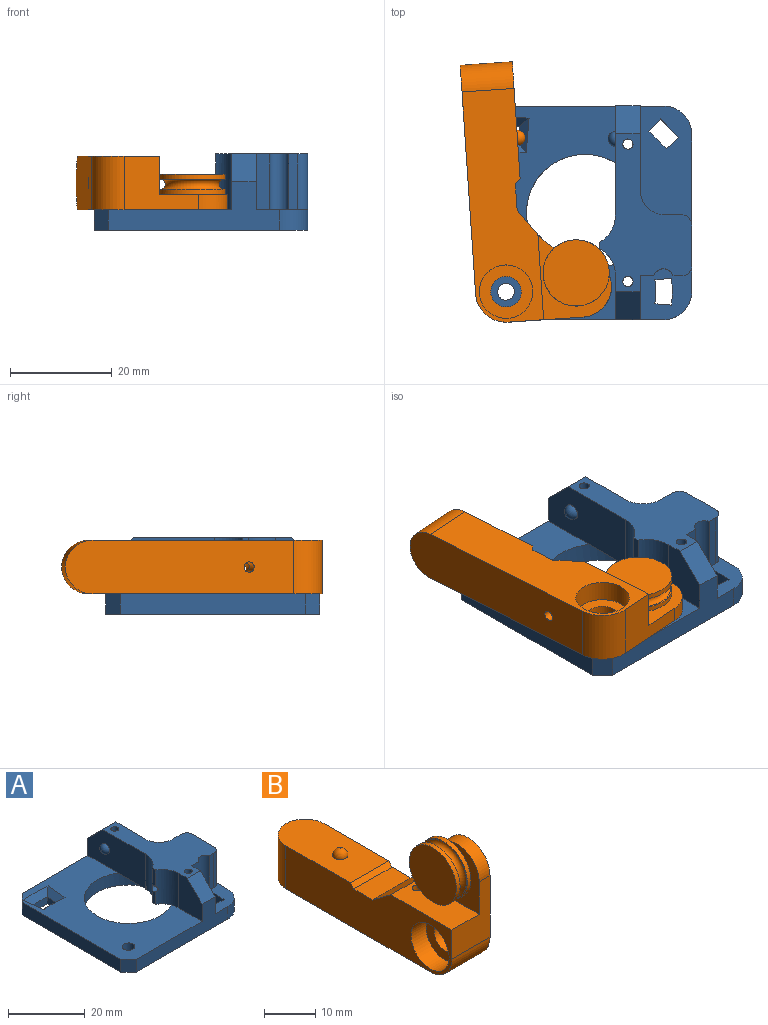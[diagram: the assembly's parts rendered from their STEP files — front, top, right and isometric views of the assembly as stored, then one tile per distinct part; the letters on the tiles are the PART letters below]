
ASSEMBLY  parts=2 mates=1
PART A: 59 faces, bbox 43.3x42.6x15.6 mm
  f0: bspline ~7.62x6.6mm, area 66.2mm2, adj f1,f18,f51,f52
  f1: bspline ~7.62x6.6mm, area 66.2mm2, adj f0,f18,f51,f52
  f2: cylinder r=1mm len=14.13mm, axis (-1,0,0), area 87.2mm2, adj f3,f4,f5,f46,f52
  f3: cylinder r=6mm len=11mm, axis (0,0,-1), area 71.3mm2, adj f2,f4,f11,f38,f45,f46
  f4: plane 5.4x1.21mm, normal (-1,0,0), area 6.4mm2, adj f2,f3,f5,f11
  f5: cylinder r=6mm len=11mm, axis (0,0,-1), area 71.3mm2, adj f2,f4,f11,f17,f38,f44,f46
  f6: plane 11x1.69mm, normal (0,-1,0), area 18.6mm2, adj f9,f11,f47,f48
  f7: plane 21.4x11mm, normal (-1,0,0), area 213.2mm2, adj f11,f12,f17,f38,f40,f41,f45
  f8: plane 16.5x11mm, normal (1,0,0), area 166.4mm2, adj f11,f12,f15,f40,f50
  f9: plane 10.6x10.15mm, normal (0,0,1), area 69.1mm2, adj f6,f13,f14,f18,f25,f34,f35,f36
  f10: plane 11x8.6mm, normal (-1,0,0), area 79.5mm2, adj f11,f13,f17,f39,f44
  f11: plane 31x18.13mm, normal (0,0,1), area 277.7mm2, adj f3,f4,f5,f6,f7,f8,f10,f14
  f12: plane 33.67x9.5mm, normal (0,1,0), area 161.1mm2, adj f7,f8,f15,f16,f17,f19,f20,f40
  f13: plane 33.67x9.5mm, normal (0,-1,0), area 161.1mm2, adj f9,f10,f14,f16,f17,f22,f25,f39
  f14: plane 11x8.6mm, normal (1,0,0), area 79.5mm2, adj f9,f11,f13,f39,f42
  f15: plane 23.4x10.15mm, normal (0,0,1), area 189.9mm2, adj f8,f12,f18,f19,f23,f30,f31,f32
  f16: plane 42x42mm, normal (0,0,-1), area 1263.2mm2, adj f12,f13,f18,f19,f20,f21,f22,f23
  f17: plane 42x27.05mm, normal (0,0,1), area 721mm2, adj f5,f7,f10,f12,f13,f20,f21,f22
  f18: plane 31.61x15.61mm, normal (1,0,0), area 184.9mm2, adj f0,f1,f9,f11,f15,f16,f19,f25
  f19: cylinder r=5.5mm len=5.5mm, axis (0,0,1), area 34.6mm2, adj f12,f15,f16,f18
  f20: plane 4x2.83mm, normal (-0.71,0.71,0), area 16mm2, adj f12,f16,f17,f21
  f21: plane 36.34x4mm, normal (-1,0,0), area 145.4mm2, adj f16,f17,f20,f22
  f22: plane 4x2.83mm, normal (-0.71,-0.71,0), area 16mm2, adj f13,f16,f17,f21
  f23: cylinder r=11.5mm len=23mm, axis (0,0,1), area 289mm2, adj f15,f16,f17,f38
  f24: cylinder r=1.65mm len=4mm, axis (0,0,1), area 41.5mm2, adj f16,f17
  f25: cylinder r=5.5mm len=5.5mm, axis (0,0,1), area 34.6mm2, adj f9,f13,f16,f18
  f26: plane 3.29x2.25mm, normal (1,0.08,0), area 7.4mm2, adj f16,f28,f29,f55
  f27: plane 3.29x2.25mm, normal (-1,0.08,0), area 7.4mm2, adj f16,f28,f29,f58
  f28: cylinder r=29.35mm len=4.73mm, axis (0,0,-1), area 10.7mm2, adj f16,f26,f27,f57
  f29: cylinder r=32.65mm len=5.27mm, axis (0,0,-1), area 11.9mm2, adj f16,f26,f27,f56
  f30: plane 4x2.46mm, normal (-0.67,0.75,0), area 13.2mm2, adj f15,f16,f32,f33
  f31: plane 4x2.46mm, normal (0.75,-0.67,0), area 13.2mm2, adj f15,f16,f32,f33
  f32: cylinder r=42.19mm len=4mm, axis (0,0,1), area 19.2mm2, adj f15,f16,f30,f31
  f33: cylinder r=45.49mm len=4mm, axis (0,0,1), area 20.8mm2, adj f15,f16,f30,f31
  f34: plane 4x3.29mm, normal (0.08,-1,0), area 13.2mm2, adj f9,f16,f36,f37
  f35: plane 4x3.29mm, normal (0.08,1,0), area 13.2mm2, adj f9,f16,f36,f37
  f36: cylinder r=29.35mm len=4.73mm, axis (0,0,-1), area 19mm2, adj f9,f16,f34,f35
  f37: cylinder r=32.65mm len=5.27mm, axis (0,0,-1), area 21.1mm2, adj f9,f16,f34,f35
  f38: plane 19.84x8.63mm, normal (0,0,-1), area 88.7mm2, adj f3,f5,f7,f23,f45,f46,f50
  f39: plane 5.5x5.5mm, normal (0,-0.71,0.71), area 37.3mm2, adj f10,f11,f13,f14
  f40: plane 5.5x5.5mm, normal (0,0.71,0.71), area 37.3mm2, adj f7,f8,f11,f12
  f41: sphere r=1.5mm, area 14.1mm2, adj f7
  f42: plane 11x2.64mm, normal (0,-1,0), area 29.1mm2, adj f9,f11,f14,f48
  f43: plane 11x3.25mm, normal (0,1,0), area 35.7mm2, adj f11,f15,f49,f50
  f44: plane 11x0.05mm, normal (0,-1,0), area 0.6mm2, adj f5,f10,f11,f17
  f45: plane 11x0.05mm, normal (0,1,0), area 0.6mm2, adj f3,f7,f11,f38
  f46: plane 4x1.21mm, normal (-1,0,0), area 4.7mm2, adj f2,f3,f5,f38
  f47: cylinder r=2mm len=11mm, axis (0,0,1), area 34.6mm2, adj f6,f9,f11,f18
  f48: cylinder r=2mm len=11mm, axis (0,0,1), area 55.7mm2, adj f6,f9,f11,f42
  f49: cylinder r=2mm len=11mm, axis (0,0,-1), area 34.6mm2, adj f11,f15,f18,f43
  f50: cylinder r=4.9mm len=11mm, axis (0,0,-1), area 84.7mm2, adj f8,f11,f15,f38,f43
  f51: cylinder r=3.3mm len=6.6mm, axis (1,0,0), area 0.5mm2, adj f0,f1,f18,f52
  f52: plane 6.5x6.48mm, normal (1,0,0), area 24mm2, adj f0,f1,f2,f51
  f53: cylinder r=1mm len=15mm, axis (0,0,1), area 94.2mm2, adj f11,f16
  f54: cylinder r=1mm len=15mm, axis (0,0,1), area 94.2mm2, adj f11,f16
  f55: plane 6.84x2.2mm, normal (0.7,0.06,0.71), area 12.5mm2, adj f17,f26,f56,f57
  f56: cone r=34.4mm half-angle=45deg, axis (0,0,1), area 17.7mm2, adj f17,f29,f55,f58
  f57: cone r=29.35mm half-angle=45deg, axis (0,0,-1), area 15.8mm2, adj f17,f28,f55,f58
  f58: plane 6.84x2.2mm, normal (-0.7,0.06,0.71), area 12.5mm2, adj f17,f27,f56,f57
PART B: 28 faces, bbox 10.5x51x27.5 mm
  f0: cylinder r=3mm len=6.37mm, axis (-1,0,0), area 120.1mm2, adj f2,f17
  f1: cylinder r=5.26mm len=10.52mm, axis (0,0,1), area 169.4mm2, adj f2,f4,f6,f10
  f2: plane 45.74x26.75mm, normal (1,0,0), area 632mm2, adj f0,f1,f5,f6,f7,f8,f9,f10
  f3: plane 16.8x7.52mm, normal (0,0,1), area 123.2mm2, adj f4,f5,f9,f14,f19
  f4: plane 45.74x13mm, normal (-1,0,0), area 419.4mm2, adj f1,f3,f5,f6,f7,f8,f9,f10
  f5: plane 14.75x10.52mm, normal (0,-1,0), area 96.9mm2, adj f2,f3,f4,f13,f14,f16
  f6: plane 45x10.52mm, normal (0,0,-1), area 458.4mm2, adj f1,f2,f4,f16,f19
  f7: plane 10.52x1mm, normal (0,-0.71,0.71), area 14.9mm2, adj f2,f4,f8,f10
  f8: plane 10.52x5.2mm, normal (0,0,1), area 54.7mm2, adj f2,f4,f7,f9
  f9: plane 10.52x5mm, normal (0,0.6,0.8), area 65.8mm2, adj f2,f3,f4,f8,f12
  f10: plane 23x10.52mm, normal (0,0,1), area 223mm2, adj f1,f2,f4,f7,f11
  f11: sphere r=1.5mm, area 14.1mm2, adj f10
  f12: cylinder r=12.52mm len=7.75mm, axis (1,0,0), area 28mm2, adj f2,f9,f13,f14,f22
  f13: cylinder r=6mm len=12mm, axis (1,0,0), area 56.5mm2, adj f2,f5,f12,f14,f22
  f14: plane 16.8x13.75mm, normal (-1,0,0), area 56.3mm2, adj f3,f5,f12,f13,f21
  f15: cylinder r=1.65mm len=3.3mm, axis (1,0,0), area 31.1mm2, adj f2,f20
  f16: cylinder r=6mm len=10.52mm, axis (-1,0,0), area 99.1mm2, adj f2,f4,f5,f6
  f17: plane 10.5x10.5mm, normal (-1,0,0), area 58.3mm2, adj f0,f18
  f18: cylinder r=5.25mm len=10.5mm, axis (-1,0,0), area 136.9mm2, adj f4,f17
  f19: cylinder r=1mm len=13mm, axis (0,0,-1), area 81.7mm2, adj f3,f6
  f20: plane 3.3x3.3mm, normal (1,0,0), area 8.6mm2, adj f15
  f21: cylinder r=6.5mm len=13mm, axis (1,0,0), area 40.8mm2, adj f14,f22,f25
  f22: plane 10.45x7.36mm, normal (1,0,0), area 26.1mm2, adj f12,f13,f21
  f23: plane 13x13mm, normal (1,0,0), area 10mm2, adj f24,f27
  f24: torus R=6.25mm, axis (-1,0,0), area 110.8mm2, adj f23,f25
  f25: plane 13x13mm, normal (-1,0,0), area 10mm2, adj f21,f24
  f26: plane 13x13mm, normal (-1,0,0), area 132.7mm2, adj f27
  f27: cylinder r=6.5mm len=13mm, axis (1,0,0), area 40.8mm2, adj f23,f26
PLACE A at identity fixed
PLACE B rot(axis=(-0.03,1,0.03),90.1deg) t=(-8.55,-8.13,5.26)mm
MATE revolute B.f18 <-> A.f24  axis (0,0,-1) through (-15.5,-9.1,0)mm
